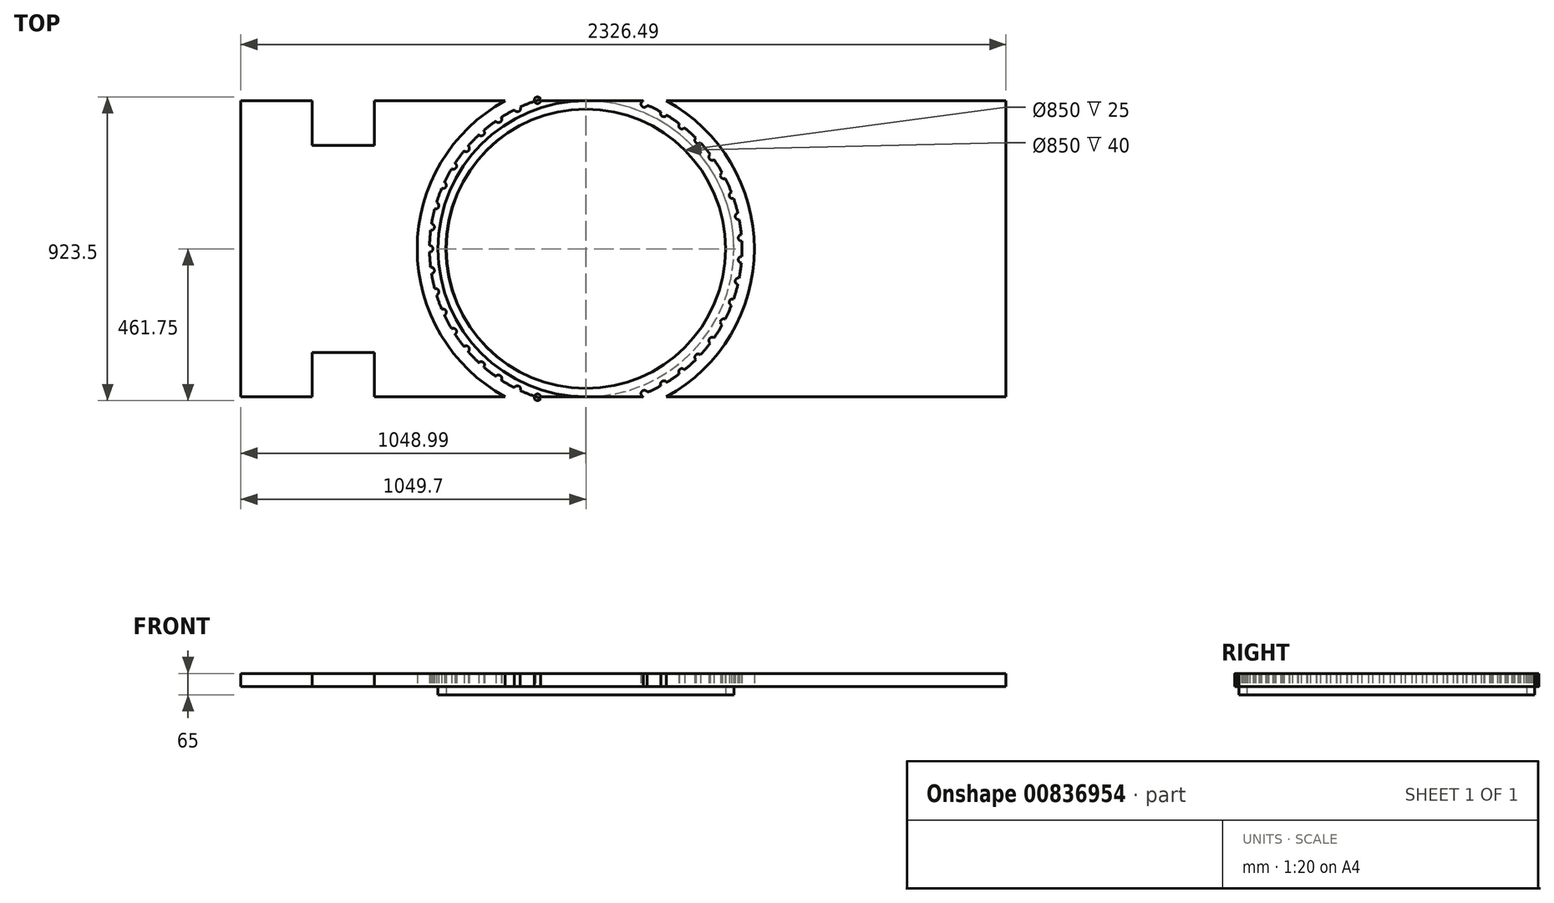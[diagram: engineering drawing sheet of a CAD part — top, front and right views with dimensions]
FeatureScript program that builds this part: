
annotation { "Feature Type Name" : "Feature", "Feature Type Description" : "" }
export const myFeature = defineFeature(function(context is Context, id is Id, definition is map)
    precondition{}
    {
        {
            var Q0;
            Q0=qCreatedBy(makeId("Top.planeOp"),FACE);
            var sketch = newSketch(context, id + "F0", { "sketchPlane" : qUnion([Q0])});
            skLineSegment(sketch, "E0.bottom", {"start": v(-1185, 450) * mm, "end": v(1185, 450) * mm});
            skLineSegment(sketch, "E0.top", {"start": v(-1185, -450) * mm, "end": v(1185, -450) * mm});
            skLineSegment(sketch, "E0.left", {"start": v(-1185, 450) * mm, "end": v(-1185, -450) * mm});
            skLineSegment(sketch, "E0.right", {"start": v(1185, 450) * mm, "end": v(1185, -450) * mm});
            skPoint(sketch, "E0.middle", {"position": v(0, 0) * mm});
            skLineSegment(sketch, "E1.bottom", {"start": v(-1185, 450) * mm, "end": v(-1141.5, 450) * mm});
            skLineSegment(sketch, "E1.top", {"start": v(-1185, -450) * mm, "end": v(-1141.5, -450) * mm});
            skLineSegment(sketch, "E1.right", {"start": v(-1141.49, 450) * mm, "end": v(-1141.49, -450) * mm});
            skLineSegment(sketch, "E2", {"start": v(1185, 0) * mm, "end": v(-1185, 0) * mm, "construction": true});
            skLineSegment(sketch, "E3", {"start": v(-92.5, -600) * mm, "end": v(-92.5, 600) * mm, "construction": true});
            skCircle(sketch, "E4", {"center": v(-92.5, 0) * mm, "radius": 600 * mm, "construction": true});
            skCircle(sketch, "E5", {"center": v(-92.5, 0) * mm, "radius": 512.5 * mm});
            skCircle(sketch, "E6", {"center": v(-92.5, 0) * mm, "radius": 425 * mm});
            skCircle(sketch, "E7", {"center": v(-92.5, 0) * mm, "radius": 475 * mm});
            skCircle(sketch, "E8", {"center": v(-567.5, 0) * mm, "radius": 10 * mm});
            skCircle(sketch, "E9.1.0", {"center": v(-562.88, -66.1) * mm, "radius": 10 * mm});
            skCircle(sketch, "E9.2.0", {"center": v(-549.1, -130.93) * mm, "radius": 10 * mm});
            skCircle(sketch, "E10.1.3.0", {"center": v(-526.43, -193.2) * mm, "radius": 10 * mm});
            skCircle(sketch, "E10.1.4.0", {"center": v(-495.32, -251.71) * mm, "radius": 10 * mm});
            skCircle(sketch, "E10.1.5.0", {"center": v(-456.37, -305.32) * mm, "radius": 10 * mm});
            skCircle(sketch, "E10.1.6.0", {"center": v(-410.34, -353) * mm, "radius": 10 * mm});
            skCircle(sketch, "E10.1.7.0", {"center": v(-358.12, -393.8) * mm, "radius": 10 * mm});
            skCircle(sketch, "E10.1.8.0", {"center": v(-300.73, -426.93) * mm, "radius": 10 * mm});
            skCircle(sketch, "E10.1.9.0", {"center": v(-239.28, -451.75) * mm, "radius": 10 * mm});
            skCircle(sketch, "E10.1.10.0", {"center": v(-174.98, -467.78) * mm, "radius": 10 * mm});
            skCircle(sketch, "E10.1.11.0", {"center": v(-109.08, -474.71) * mm, "radius": 10 * mm});
            skCircle(sketch, "E10.1.12.0", {"center": v(-42.85, -472.4) * mm, "radius": 10 * mm});
            skCircle(sketch, "E10.1.13.0", {"center": v(22.41, -460.9) * mm, "radius": 10 * mm});
            skCircle(sketch, "E10.1.14.0", {"center": v(85.44, -440.41) * mm, "radius": 10 * mm});
            skCircle(sketch, "E10.1.15.0", {"center": v(145, -411.36) * mm, "radius": 10 * mm});
            skCircle(sketch, "E10.1.16.0", {"center": v(199.94, -374.3) * mm, "radius": 10 * mm});
            skCircle(sketch, "E10.1.17.0", {"center": v(249.19, -329.96) * mm, "radius": 10 * mm});
            skCircle(sketch, "E10.1.18.0", {"center": v(291.78, -279.2) * mm, "radius": 10 * mm});
            skCircle(sketch, "E10.1.19.0", {"center": v(326.9, -223) * mm, "radius": 10 * mm});
            skCircle(sketch, "E10.1.20.0", {"center": v(353.85, -162.46) * mm, "radius": 10 * mm});
            skCircle(sketch, "E10.1.21.0", {"center": v(372.12, -98.76) * mm, "radius": 10 * mm});
            skCircle(sketch, "E10.1.22.0", {"center": v(381.34, -33.13) * mm, "radius": 10 * mm});
            skCircle(sketch, "E10.1.23.0", {"center": v(381.34, 33.13) * mm, "radius": 10 * mm});
            skCircle(sketch, "E10.1.24.0", {"center": v(372.12, 98.76) * mm, "radius": 10 * mm});
            skCircle(sketch, "E10.1.25.0", {"center": v(353.85, 162.46) * mm, "radius": 10 * mm});
            skCircle(sketch, "E10.1.26.0", {"center": v(326.9, 223) * mm, "radius": 10 * mm});
            skCircle(sketch, "E10.1.27.0", {"center": v(291.78, 279.2) * mm, "radius": 10 * mm});
            skCircle(sketch, "E10.1.28.0", {"center": v(249.19, 329.96) * mm, "radius": 10 * mm});
            skCircle(sketch, "E10.1.29.0", {"center": v(199.94, 374.3) * mm, "radius": 10 * mm});
            skCircle(sketch, "E10.1.30.0", {"center": v(145, 411.36) * mm, "radius": 10 * mm});
            skCircle(sketch, "E10.1.31.0", {"center": v(85.44, 440.41) * mm, "radius": 10 * mm});
            skCircle(sketch, "E10.1.32.0", {"center": v(22.41, 460.9) * mm, "radius": 10 * mm});
            skCircle(sketch, "E10.1.33.0", {"center": v(-42.85, 472.4) * mm, "radius": 10 * mm});
            skCircle(sketch, "E10.1.34.0", {"center": v(-109.08, 474.71) * mm, "radius": 10 * mm});
            skCircle(sketch, "E10.1.35.0", {"center": v(-174.98, 467.78) * mm, "radius": 10 * mm});
            skCircle(sketch, "E10.1.36.0", {"center": v(-239.28, 451.75) * mm, "radius": 10 * mm});
            skCircle(sketch, "E10.1.37.0", {"center": v(-300.73, 426.93) * mm, "radius": 10 * mm});
            skCircle(sketch, "E10.1.38.0", {"center": v(-358.12, 393.8) * mm, "radius": 10 * mm});
            skCircle(sketch, "E10.1.39.0", {"center": v(-410.34, 353) * mm, "radius": 10 * mm});
            skCircle(sketch, "E10.1.40.0", {"center": v(-456.37, 305.32) * mm, "radius": 10 * mm});
            skCircle(sketch, "E10.1.41.0", {"center": v(-495.32, 251.71) * mm, "radius": 10 * mm});
            skCircle(sketch, "E10.1.42.0", {"center": v(-526.43, 193.2) * mm, "radius": 10 * mm});
            skCircle(sketch, "E10.1.43.0", {"center": v(-549.1, 130.93) * mm, "radius": 10 * mm});
            skCircle(sketch, "E10.1.44.0", {"center": v(-562.88, 66.1) * mm, "radius": 10 * mm});
            skCircle(sketch, "E11", {"center": v(-92.5, 0) * mm, "radius": 370 * mm});
            skCircle(sketch, "E12", {"center": v(-462.5, 0) * mm, "radius": 10 * mm});
            skCircle(sketch, "E13.1.0", {"center": v(-458.9, -51.5) * mm, "radius": 10 * mm});
            skCircle(sketch, "E13.2.0", {"center": v(-448.17, -101.99) * mm, "radius": 10 * mm});
            skCircle(sketch, "E13.3.0", {"center": v(-430.51, -150.5) * mm, "radius": 10 * mm});
            skCircle(sketch, "E13.4.0", {"center": v(-406.28, -196.07) * mm, "radius": 10 * mm});
            skCircle(sketch, "E13.5.0", {"center": v(-375.94, -237.83) * mm, "radius": 10 * mm});
            skCircle(sketch, "E13.6.0", {"center": v(-340.08, -274.96) * mm, "radius": 10 * mm});
            skCircle(sketch, "E13.7.0", {"center": v(-299.4, -306.74) * mm, "radius": 10 * mm});
            skCircle(sketch, "E13.8.0", {"center": v(-254.7, -332.55) * mm, "radius": 10 * mm});
            skCircle(sketch, "E13.9.0", {"center": v(-206.84, -351.9) * mm, "radius": 10 * mm});
            skCircle(sketch, "E13.10.0", {"center": v(-156.75, -364.38) * mm, "radius": 10 * mm});
            skCircle(sketch, "E13.11.0", {"center": v(-105.41, -369.77) * mm, "radius": 10 * mm});
            skCircle(sketch, "E13.12.0", {"center": v(-53.82, -367.97) * mm, "radius": 10 * mm});
            skCircle(sketch, "E13.13.0", {"center": v(-2.99, -359) * mm, "radius": 10 * mm});
            skCircle(sketch, "E13.14.0", {"center": v(46.1, -343.06) * mm, "radius": 10 * mm});
            skCircle(sketch, "E13.15.0", {"center": v(92.5, -320.43) * mm, "radius": 10 * mm});
            skCircle(sketch, "E13.16.0", {"center": v(135.3, -291.56) * mm, "radius": 10 * mm});
            skCircle(sketch, "E13.17.0", {"center": v(173.66, -257.02) * mm, "radius": 10 * mm});
            skCircle(sketch, "E13.18.0", {"center": v(206.84, -217.48) * mm, "radius": 10 * mm});
            skCircle(sketch, "E13.19.0", {"center": v(234.2, -173.7) * mm, "radius": 10 * mm});
            skCircle(sketch, "E13.20.0", {"center": v(255.19, -126.55) * mm, "radius": 10 * mm});
            skCircle(sketch, "E13.21.0", {"center": v(269.41, -76.93) * mm, "radius": 10 * mm});
            skCircle(sketch, "E13.22.0", {"center": v(276.6, -25.8) * mm, "radius": 10 * mm});
            skCircle(sketch, "E13.23.0", {"center": v(276.6, 25.8) * mm, "radius": 10 * mm});
            skCircle(sketch, "E13.24.0", {"center": v(269.41, 76.93) * mm, "radius": 10 * mm});
            skCircle(sketch, "E13.25.0", {"center": v(255.19, 126.55) * mm, "radius": 10 * mm});
            skCircle(sketch, "E13.26.0", {"center": v(234.2, 173.7) * mm, "radius": 10 * mm});
            skCircle(sketch, "E13.27.0", {"center": v(206.84, 217.48) * mm, "radius": 10 * mm});
            skCircle(sketch, "E13.28.0", {"center": v(173.66, 257.02) * mm, "radius": 10 * mm});
            skCircle(sketch, "E13.29.0", {"center": v(135.3, 291.56) * mm, "radius": 10 * mm});
            skCircle(sketch, "E13.30.0", {"center": v(92.5, 320.43) * mm, "radius": 10 * mm});
            skCircle(sketch, "E13.31.0", {"center": v(46.1, 343.06) * mm, "radius": 10 * mm});
            skCircle(sketch, "E13.32.0", {"center": v(-2.99, 359) * mm, "radius": 10 * mm});
            skCircle(sketch, "E13.33.0", {"center": v(-53.82, 367.97) * mm, "radius": 10 * mm});
            skCircle(sketch, "E13.34.0", {"center": v(-105.41, 369.77) * mm, "radius": 10 * mm});
            skCircle(sketch, "E13.35.0", {"center": v(-156.75, 364.38) * mm, "radius": 10 * mm});
            skCircle(sketch, "E13.36.0", {"center": v(-206.84, 351.9) * mm, "radius": 10 * mm});
            skCircle(sketch, "E13.37.0", {"center": v(-254.7, 332.55) * mm, "radius": 10 * mm});
            skCircle(sketch, "E13.38.0", {"center": v(-299.4, 306.74) * mm, "radius": 10 * mm});
            skCircle(sketch, "E13.39.0", {"center": v(-340.08, 274.96) * mm, "radius": 10 * mm});
            skCircle(sketch, "E13.40.0", {"center": v(-375.94, 237.83) * mm, "radius": 10 * mm});
            skCircle(sketch, "E13.41.0", {"center": v(-406.28, 196.07) * mm, "radius": 10 * mm});
            skCircle(sketch, "E13.42.0", {"center": v(-430.51, 150.5) * mm, "radius": 10 * mm});
            skCircle(sketch, "E13.43.0", {"center": v(-448.17, 101.99) * mm, "radius": 10 * mm});
            skCircle(sketch, "E13.44.0", {"center": v(-458.9, 51.5) * mm, "radius": 10 * mm});
            skLineSegment(sketch, "E14.bottom", {"start": v(-925, 450) * mm, "end": v(-735, 450) * mm});
            skLineSegment(sketch, "E14.top", {"start": v(-925, 315) * mm, "end": v(-735, 315) * mm});
            skLineSegment(sketch, "E14.left", {"start": v(-925, 450) * mm, "end": v(-925, 315) * mm});
            skLineSegment(sketch, "E14.right", {"start": v(-735, 450) * mm, "end": v(-735, 315) * mm});
            skLineSegment(sketch, "E15.bottom", {"start": v(-913, 327) * mm, "end": v(-747, 327) * mm});
            skLineSegment(sketch, "E15.top", {"start": v(-913, 438) * mm, "end": v(-747, 438) * mm});
            skLineSegment(sketch, "E15.left", {"start": v(-913, 327) * mm, "end": v(-913, 438) * mm});
            skLineSegment(sketch, "E15.right", {"start": v(-747, 327) * mm, "end": v(-747, 438) * mm});
            skPoint(sketch, "E15.middle", {"position": v(-830, 382.5) * mm});
            skLineSegment(sketch, "E16.MirrorCS", {"start": v(-735, -450) * mm, "end": v(-735, -315) * mm});
            skLineSegment(sketch, "E17.MirrorCS", {"start": v(-925, -315) * mm, "end": v(-735, -315) * mm});
            skLineSegment(sketch, "E18.MirrorCS", {"start": v(-913, -438) * mm, "end": v(-747, -438) * mm});
            skLineSegment(sketch, "E19.MirrorCS", {"start": v(-925, -450) * mm, "end": v(-925, -315) * mm});
            skLineSegment(sketch, "E20.MirrorCS", {"start": v(-747, -327) * mm, "end": v(-747, -438) * mm});
            skPoint(sketch, "E21.MirrorP", {"position": v(-830, -382.5) * mm});
            skLineSegment(sketch, "E22.MirrorCS", {"start": v(-913, -327) * mm, "end": v(-913, -438) * mm});
            skLineSegment(sketch, "E23.MirrorCS", {"start": v(-913, -327) * mm, "end": v(-747, -327) * mm});
            skLineSegment(sketch, "E24.MirrorCS", {"start": v(-925, -450) * mm, "end": v(-735, -450) * mm});
            skArc(sketch, "E25", {"start": v(-301.83, -562.3) * mm, "mid": v(-739.86, -478.19) * mm, "end": v(-1185, -450) * mm});
            skArc(sketch, "E26.MirrorCS", {"start": v(-301.83, 562.3) * mm, "mid": v(-739.86, 478.19) * mm, "end": v(-1185, 450) * mm});
            skCircle(sketch, "E27", {"center": v(-92.5, 0) * mm, "radius": 325 * mm});
            skSolve(sketch);
        }
        {
            var Q0;
            {var subQ0=sQuery(id+"F0.wireOp",EDGE,"E10.1.36.0");var subQ1=sQuery(id+"F0.wireOp",EDGE,"E0.bottom");var subQ2=makeQuery(id+"F0.imprint","INTERSECT",VERTEX,{"disambiguationData":[OD(0.0)],"derivedFrom":[subQ1,subQ0]});Q0=makeQuery(id+"F0.imprint","IMPRINT",FACE,{"disambiguationData":[TD([[makeQuery(id+"F0.imprint","IMPRINT",EDGE,{"disambiguationData":[TD([[subQ2,-1.0]])],"derivedFrom":subQ1}),-1.0]])]});}
            var Q1;
            {var subQ0=sQuery(id+"F0.wireOp",EDGE,"E7");var subQ1=sQuery(id+"F0.wireOp",EDGE,"E0.bottom");var subQ2=makeQuery(id+"F0.imprint","INTERSECT",VERTEX,{"disambiguationData":[OD(1.0)],"derivedFrom":[subQ1,subQ0]});Q1=makeQuery(id+"F0.imprint","IMPRINT",FACE,{"disambiguationData":[TD([[makeQuery(id+"F0.imprint","IMPRINT",EDGE,{"disambiguationData":[TD([[subQ2,-1.0]])],"derivedFrom":subQ1}),-1.0]])]});}
            var Q2;
            {var subQ38=sQuery(id+"F0.wireOp",EDGE,"E5");var subQ39=sQuery(id+"F0.wireOp",EDGE,"E0.bottom");var subQ40=makeQuery(id+"F0.imprint","INTERSECT",VERTEX,{"disambiguationData":[OD(0.0)],"derivedFrom":[subQ39,subQ38]});Q2=makeQuery(id+"F0.imprint","IMPRINT",FACE,{"disambiguationData":[TD([[makeQuery(id+"F0.imprint","IMPRINT",EDGE,{"disambiguationData":[TD([[subQ40,-1.0]])],"derivedFrom":subQ39}),-1.0]])]});}
            var Q3;
            {var subQ11=sQuery(id+"F0.wireOp",EDGE,"E5");var subQ12=sQuery(id+"F0.wireOp",EDGE,"E0.bottom");var subQ18=makeQuery(id+"F0.imprint","INTERSECT",VERTEX,{"disambiguationData":[OD(0.0)],"derivedFrom":[subQ12,subQ11]});Q3=makeQuery(id+"F0.imprint","IMPRINT",FACE,{"disambiguationData":[TD([[makeQuery(id+"F0.imprint","IMPRINT",EDGE,{"disambiguationData":[TD([[subQ18,-1.0]])],"derivedFrom":subQ12}),1.0]])]});}
            var Q4;
            {var subQ1=sQuery(id+"F0.wireOp",EDGE,"E0.top");var subQ15=sQuery(id+"F0.wireOp",EDGE,"E5");var subQ16=makeQuery(id+"F0.imprint","INTERSECT",VERTEX,{"disambiguationData":[OD(0.0)],"derivedFrom":[subQ1,subQ15]});Q4=makeQuery(id+"F0.imprint","IMPRINT",FACE,{"disambiguationData":[TD([[makeQuery(id+"F0.imprint","IMPRINT",EDGE,{"disambiguationData":[TD([[subQ16,-1.0]])],"derivedFrom":subQ1}),-1.0]])]});}
            var Q5;
            {var subQ35=sQuery(id+"F0.wireOp",EDGE,"E5");var subQ36=sQuery(id+"F0.wireOp",EDGE,"E0.bottom");var subQ37=makeQuery(id+"F0.imprint","INTERSECT",VERTEX,{"disambiguationData":[OD(1.0)],"derivedFrom":[subQ36,subQ35]});Q5=makeQuery(id+"F0.imprint","IMPRINT",FACE,{"disambiguationData":[TD([[makeQuery(id+"F0.imprint","IMPRINT",EDGE,{"disambiguationData":[TD([[subQ37,1.0]])],"derivedFrom":subQ36}),-1.0]])]});}
            var Q6;
            Q6=makeQuery(id+"F0.imprint","IMPRINT",FACE,{"disambiguationData":[TD([[makeQuery(id+"F0.imprint","IMPRINT",EDGE,{"derivedFrom":sQuery(id+"F0.wireOp",EDGE,"E6")}),-1.0]])]});
            var Q7;
            {var subQ7=sQuery(id+"F0.wireOp",EDGE,"E10.1.36.0");var subQ12=sQuery(id+"F0.wireOp",EDGE,"E0.bottom");var subQ13=makeQuery(id+"F0.imprint","INTERSECT",VERTEX,{"disambiguationData":[OD(1.0)],"derivedFrom":[subQ12,subQ7]});Q7=makeQuery(id+"F0.imprint","IMPRINT",FACE,{"disambiguationData":[TD([[makeQuery(id+"F0.imprint","IMPRINT",EDGE,{"disambiguationData":[TD([[subQ13,-1.0]])],"derivedFrom":subQ12}),1.0]])]});}
            var Q8;
            {var subQ4=sQuery(id+"F0.wireOp",EDGE,"E0.top");var subQ14=sQuery(id+"F0.wireOp",EDGE,"E10.1.9.0");var subQ15=makeQuery(id+"F0.imprint","INTERSECT",VERTEX,{"disambiguationData":[OD(1.0)],"derivedFrom":[subQ4,subQ14]});Q8=makeQuery(id+"F0.imprint","IMPRINT",FACE,{"disambiguationData":[TD([[makeQuery(id+"F0.imprint","IMPRINT",EDGE,{"disambiguationData":[TD([[subQ15,-1.0]])],"derivedFrom":subQ4}),-1.0]])]});}
            var Q9;
            {var subQ0=sQuery(id+"F0.wireOp",EDGE,"E7");var subQ1=sQuery(id+"F0.wireOp",EDGE,"E0.top");var subQ2=makeQuery(id+"F0.imprint","INTERSECT",VERTEX,{"disambiguationData":[OD(1.0)],"derivedFrom":[subQ1,subQ0]});Q9=makeQuery(id+"F0.imprint","IMPRINT",FACE,{"disambiguationData":[TD([[makeQuery(id+"F0.imprint","IMPRINT",EDGE,{"disambiguationData":[TD([[subQ2,-1.0]])],"derivedFrom":subQ1}),1.0]])]});}
            extrude(context, id + "F1", {"entities" : qUnion([Q0, Q1, Q2, Q3, Q4, Q5, Q6, Q7, Q8, Q9]), "depth" : 40 * mm, "offsetDistance" : 25 * mm});
        }
        {
            var Q0;
            Q0=qCreatedBy(makeId("Front.planeOp"),FACE);
            var sketch = newSketch(context, id + "F2", { "sketchPlane" : qUnion([Q0])});
            skLineSegment(sketch, "E28.left", {"start": v(333.2, 0) * mm, "end": v(333.2, -25) * mm});
            skLineSegment(sketch, "E29", {"start": v(-91.8, 0) * mm, "end": v(-91.8, 104.82) * mm, "construction": true});
            skLineSegment(sketch, "E30.top", {"start": v(333.2, -25) * mm, "end": v(358.2, -25) * mm});
            skLineSegment(sketch, "E30.right", {"start": v(358.2, 0) * mm, "end": v(358.2, -25) * mm});
            skLineSegment(sketch, "E31", {"start": v(333.2, 0) * mm, "end": v(358.2, 0) * mm});
            skSolve(sketch);
        }
        {
            var Q0;
            Q0 = qSketchRegion(id + "F2", true);
            var Q1;
            Q1=sQuery(id+"F2.wireOp",EDGE,"E29");
            revolve(context, id + "F3", {"surfaceOperationType" : NewSurfaceOperationType.NEW, "entities" : qUnion([Q0]), "axis" : qUnion([Q1]), "revolveType" : RevolveType.FULL});
        }
    });
